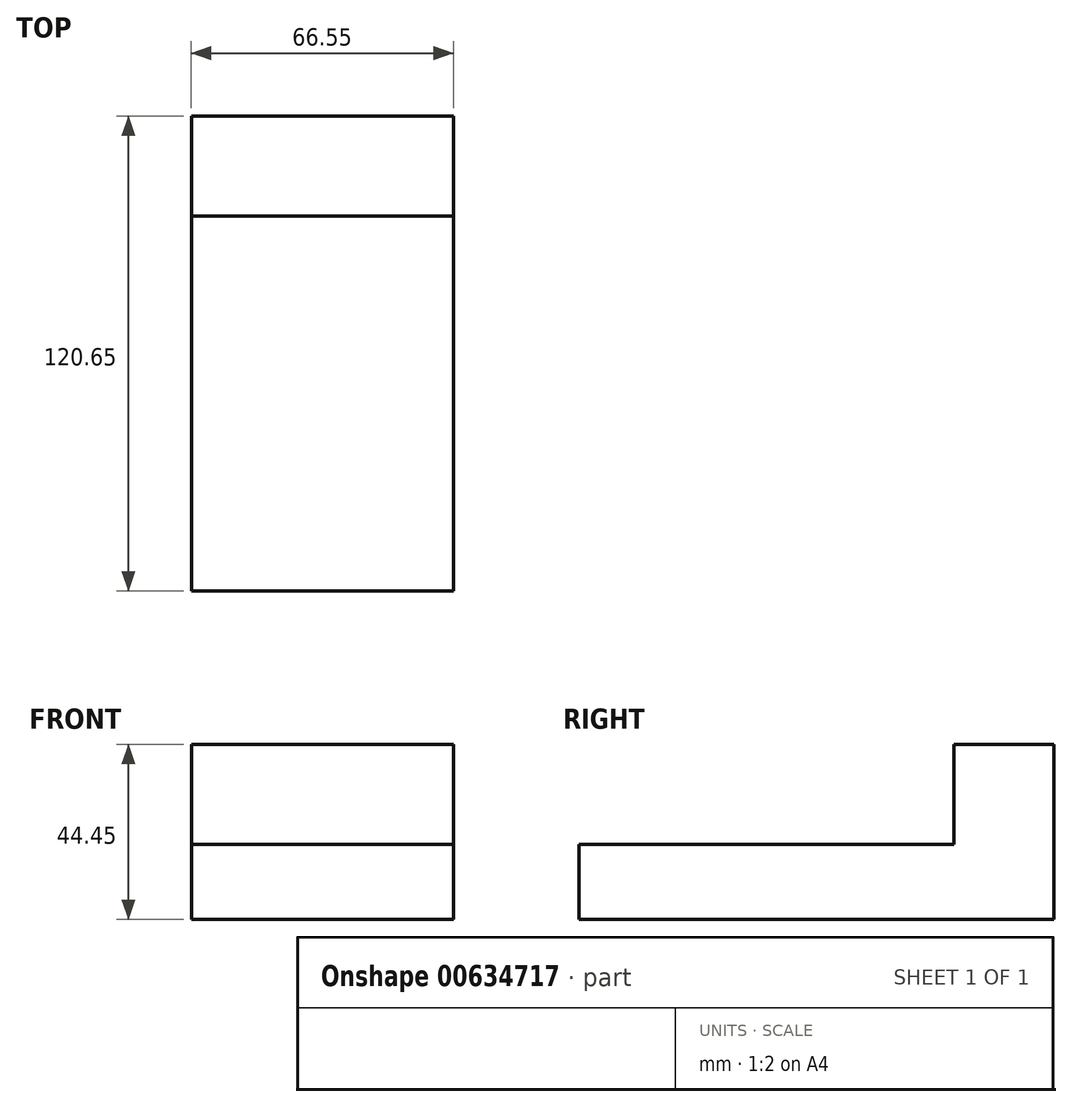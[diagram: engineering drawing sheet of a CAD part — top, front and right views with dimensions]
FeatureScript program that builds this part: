
annotation { "Feature Type Name" : "Feature", "Feature Type Description" : "" }
export const myFeature = defineFeature(function(context is Context, id is Id, definition is map)
    precondition{}
    {
        {
            var Q0;
            Q0=qCreatedBy(makeId("Front.planeOp"),FACE);
            var sketch = newSketch(context, id + "F0", { "sketchPlane" : qUnion([Q0])});
            skLineSegment(sketch, "E0", {"start": v(0, 0) * mm, "end": v(0, 44.45) * mm});
            skLineSegment(sketch, "E1", {"start": v(0, 44.45) * mm, "end": v(-66.55, 44.45) * mm});
            skLineSegment(sketch, "E2", {"start": v(-66.55, 44.45) * mm, "end": v(-66.55, 0) * mm});
            skLineSegment(sketch, "E3", {"start": v(-66.55, 0) * mm, "end": v(0, 0) * mm});
            skSolve(sketch);
        }
        {
            var Q0;
            Q0 = qSketchRegion(id + "F0", true);
            extrude(context, id + "F1", {"entities" : qUnion([Q0]), "depth" : 25.4 * mm, "offsetDistance" : 25.4 * mm});
        }
        {
            var Q0;
            Q0=makeQuery(id+"F1.opExtrude","CAP_FACE",FACE,{"disambiguationData":[OSD([sQuery(id+"F0.wireOp",EDGE,"E0"),sQuery(id+"F0.wireOp",EDGE,"E1"),sQuery(id+"F0.wireOp",EDGE,"E2"),sQuery(id+"F0.wireOp",EDGE,"E3")])],"isStart":false});
            var sketch = newSketch(context, id + "F2", { "sketchPlane" : qUnion([Q0])});
            skLineSegment(sketch, "E4", {"start": v(-66.55, 0) * mm, "end": v(-66.55, 19.05) * mm});
            skLineSegment(sketch, "E5", {"start": v(-66.55, 19.05) * mm, "end": v(0, 19.05) * mm});
            skPoint(sketch, "E5.endSnap0", {"position": v(0, 22.23) * mm});
            skLineSegment(sketch, "E6", {"start": v(0, 19.05) * mm, "end": v(0, 0) * mm});
            skLineSegment(sketch, "E7", {"start": v(0, 0) * mm, "end": v(-66.55, 0) * mm});
            skSolve(sketch);
        }
        {
            var Q0;
            Q0=makeQuery(id+"F2.imprint","IMPRINT",FACE,{"disambiguationData":[TD([[makeQuery(id+"F2.imprint","IMPRINT",EDGE,{"derivedFrom":sQuery(id+"F2.wireOp",EDGE,"E4")}),1.0]])]});
            extrude(context, id + "F3", {"entities" : qUnion([Q0]), "operationType" : NewBodyOperationType.ADD, "depth" : 95.25 * mm, "offsetDistance" : 25.4 * mm});
        }
    });
